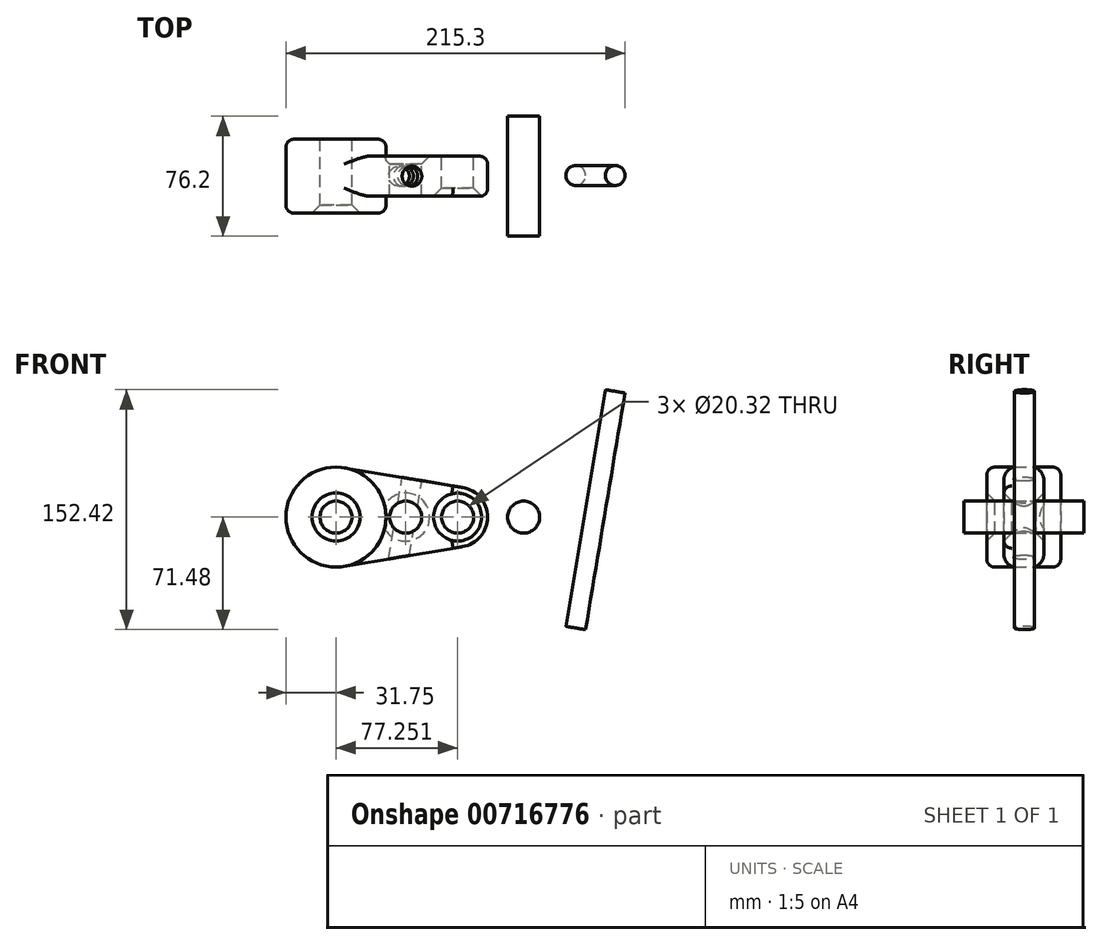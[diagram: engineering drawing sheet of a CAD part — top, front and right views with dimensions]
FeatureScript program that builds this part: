
annotation { "Feature Type Name" : "Feature", "Feature Type Description" : "" }
export const myFeature = defineFeature(function(context is Context, id is Id, definition is map)
    precondition{}
    {
        {
            var Q0;
            Q0=qCreatedBy(makeId("Front.planeOp"),FACE);
            var sketch = newSketch(context, id + "F0", { "sketchPlane" : qUnion([Q0])});
            skCircle(sketch, "E0", {"center": v(0, 0) * mm, "radius": 31.75 * mm});
            skCircle(sketch, "E1", {"center": v(77.25, 0) * mm, "radius": 19.05 * mm});
            skCircle(sketch, "E2", {"center": v(0, 0) * mm, "radius": 10.16 * mm});
            skCircle(sketch, "E3", {"center": v(77.25, 0) * mm, "radius": 10.16 * mm});
            skLineSegment(sketch, "E4", {"start": v(5.22, 31.32) * mm, "end": v(80.38, 18.8) * mm});
            skLineSegment(sketch, "E5", {"start": v(80.38, -18.8) * mm, "end": v(5.22, -31.32) * mm});
            skCircle(sketch, "E6", {"center": v(44.23, 0) * mm, "radius": 10.16 * mm});
            skCircle(sketch, "E7", {"center": v(119.16, 0) * mm, "radius": 10.16 * mm});
            skSolve(sketch);
        }
        {
            var Q0;
            {var subQ1=sQuery(id+"F0.wireOp",EDGE,"E4");Q0=makeQuery(id+"F0.imprint","IMPRINT",FACE,{"disambiguationData":[TD([[makeQuery(id+"F0.imprint","IMPRINT",EDGE,{"derivedFrom":subQ1}),-1.0]])]});}
            var Q1;
            Q1=makeQuery(id+"F0.imprint","IMPRINT",FACE,{"disambiguationData":[TD([[makeQuery(id+"F0.imprint","IMPRINT",EDGE,{"derivedFrom":sQuery(id+"F0.wireOp",EDGE,"E3")}),-1.0]])]});
            extrude(context, id + "F1", {"entities" : qUnion([Q0, Q1]), "endBound" : BoundingType.SYMMETRIC, "depth" : 25.4 * mm, "offsetDistance" : 25.4 * mm});
        }
        {
            var Q0;
            Q0=makeQuery(id+"F1.opExtrude","CAP_EDGE",EDGE,{"disambiguationData":[OSD([sQuery(id+"F0.wireOp",EDGE,"E3")])],"isStart":false});
            var Q1;
            Q1=makeQuery(id+"F1.opExtrude","CAP_EDGE",EDGE,{"disambiguationData":[OSD([sQuery(id+"F0.wireOp",EDGE,"E2")])],"isStart":false});
            chamfer(context, id + "F2", {"entities" : qUnion([Q0, Q1]), "width" : 5.08 * mm, "tangentPropagation" : true});
        }
        {
            var Q0;
            Q0=makeQuery(id+"F0.imprint","IMPRINT",FACE,{"disambiguationData":[TD([[makeQuery(id+"F0.imprint","IMPRINT",EDGE,{"derivedFrom":sQuery(id+"F0.wireOp",EDGE,"E2")}),-1.0]])]});
            extrude(context, id + "F3", {"entities" : qUnion([Q0]), "operationType" : NewBodyOperationType.ADD, "endBound" : BoundingType.SYMMETRIC, "depth" : 47 * mm, "offsetDistance" : 25.4 * mm});
        }
        {
            var Q0;
            Q0=makeQuery(id+"F3.opExtrude","CAP_EDGE",EDGE,{"disambiguationData":[OSD([sQuery(id+"F0.wireOp",EDGE,"E2")])],"isStart":false});
            chamfer(context, id + "F4", {"entities" : qUnion([Q0]), "width" : 5.08 * mm, "tangentPropagation" : true});
        }
        {
            var Q0;
            Q0=makeQuery(id+"F1.opExtrude","CAP_EDGE",EDGE,{"disambiguationData":[OSD([sQuery(id+"F0.wireOp",EDGE,"E5")])],"isStart":false});
            var Q1;
            Q1=makeQuery(id+"F3.opExtrude","CAP_EDGE",EDGE,{"disambiguationData":[OSD([sQuery(id+"F0.wireOp",EDGE,"E0")])],"isStart":false});
            var Q2;
            Q2=makeQuery(id+"F3.opExtrude","CAP_EDGE",EDGE,{"disambiguationData":[OSD([sQuery(id+"F0.wireOp",EDGE,"E0")])],"isStart":true});
            var Q3;
            Q3=makeQuery(id+"F1.opExtrude","CAP_EDGE",EDGE,{"disambiguationData":[OSD([sQuery(id+"F0.wireOp",EDGE,"E5")])],"isStart":true});
            var Q4;
            Q4=makeQuery(id+"F1.opExtrude","CAP_EDGE",EDGE,{"disambiguationData":[OSD([sQuery(id+"F0.wireOp",EDGE,"E1")])],"isStart":true});
            fillet(context, id + "F5", {"entities" : qUnion([Q0, Q1, Q2, Q3, Q4]), "radius" : 5.08 * mm, "tangentPropagation" : true, "allowEdgeOverflow" : false});
        }
        {
            var Q0;
            Q0=makeQuery(id+"F1.opExtrude","CAP_EDGE",EDGE,{"disambiguationData":[OSD([sQuery(id+"F0.wireOp",EDGE,"E6")])],"isStart":true});
            chamfer(context, id + "F6", {"entities" : qUnion([Q0]), "width" : 5.08 * mm, "tangentPropagation" : true});
        }
        {
            var Q0;
            Q0=makeQuery(id+"F0.imprint","IMPRINT",FACE,{"disambiguationData":[TD([[makeQuery(id+"F0.imprint","IMPRINT",EDGE,{"derivedFrom":sQuery(id+"F0.wireOp",EDGE,"E7")}),1.0]])]});
            extrude(context, id + "F7", {"entities" : qUnion([Q0]), "endBound" : BoundingType.SYMMETRIC, "depth" : 76.2 * mm, "offsetDistance" : 25.4 * mm});
        }
        {
            var Q0;
            Q0=makeQuery(id+"F1.opExtrude","SWEPT_FACE",FACE,{"disambiguationData":[OSD([sQuery(id+"F0.wireOp",EDGE,"E4")])]});
            var sketch = newSketch(context, id + "F8", { "sketchPlane" : qUnion([Q0])});
            skCircle(sketch, "E8", {"center": v(43.63, 0) * mm, "radius": 6.35 * mm});
            skCircle(sketch, "E9", {"center": v(161.74, 0.45) * mm, "radius": 6.35 * mm});
            skSolve(sketch);
        }
        {
            var Q0;
            Q0=makeQuery(id+"F8.imprint","IMPRINT",FACE,{"disambiguationData":[TD([[makeQuery(id+"F8.imprint","IMPRINT",EDGE,{"derivedFrom":sQuery(id+"F8.wireOp",EDGE,"E8")}),1.0]])]});
            var Q1;
            Q1=sQuery(id+"F8.wireOp",EDGE,"E8");
            extrude(context, id + "F9", {"entities" : qUnion([Q0]), "operationType" : NewBodyOperationType.REMOVE, "surfaceOperationType" : NewSurfaceOperationType.ADD, "surfaceEntities" : qUnion([Q1]), "endBound" : BoundingType.THROUGH_ALL, "oppositeDirection" : true, "depth" : 25.4 * mm, "offsetDistance" : 25.4 * mm});
        }
        {
            var Q0;
            Q0=makeQuery(id+"F8.imprint","IMPRINT",FACE,{"disambiguationData":[TD([[makeQuery(id+"F8.imprint","IMPRINT",EDGE,{"derivedFrom":sQuery(id+"F8.wireOp",EDGE,"E9")}),1.0]])]});
            var Q1;
            Q1=sQuery(id+"F8.wireOp",EDGE,"E9");
            extrude(context, id + "F10", {"entities" : qUnion([Q0]), "surfaceEntities" : qUnion([Q1]), "endBound" : BoundingType.SYMMETRIC, "depth" : 152.4 * mm, "offsetDistance" : 25.4 * mm});
        }
    });
